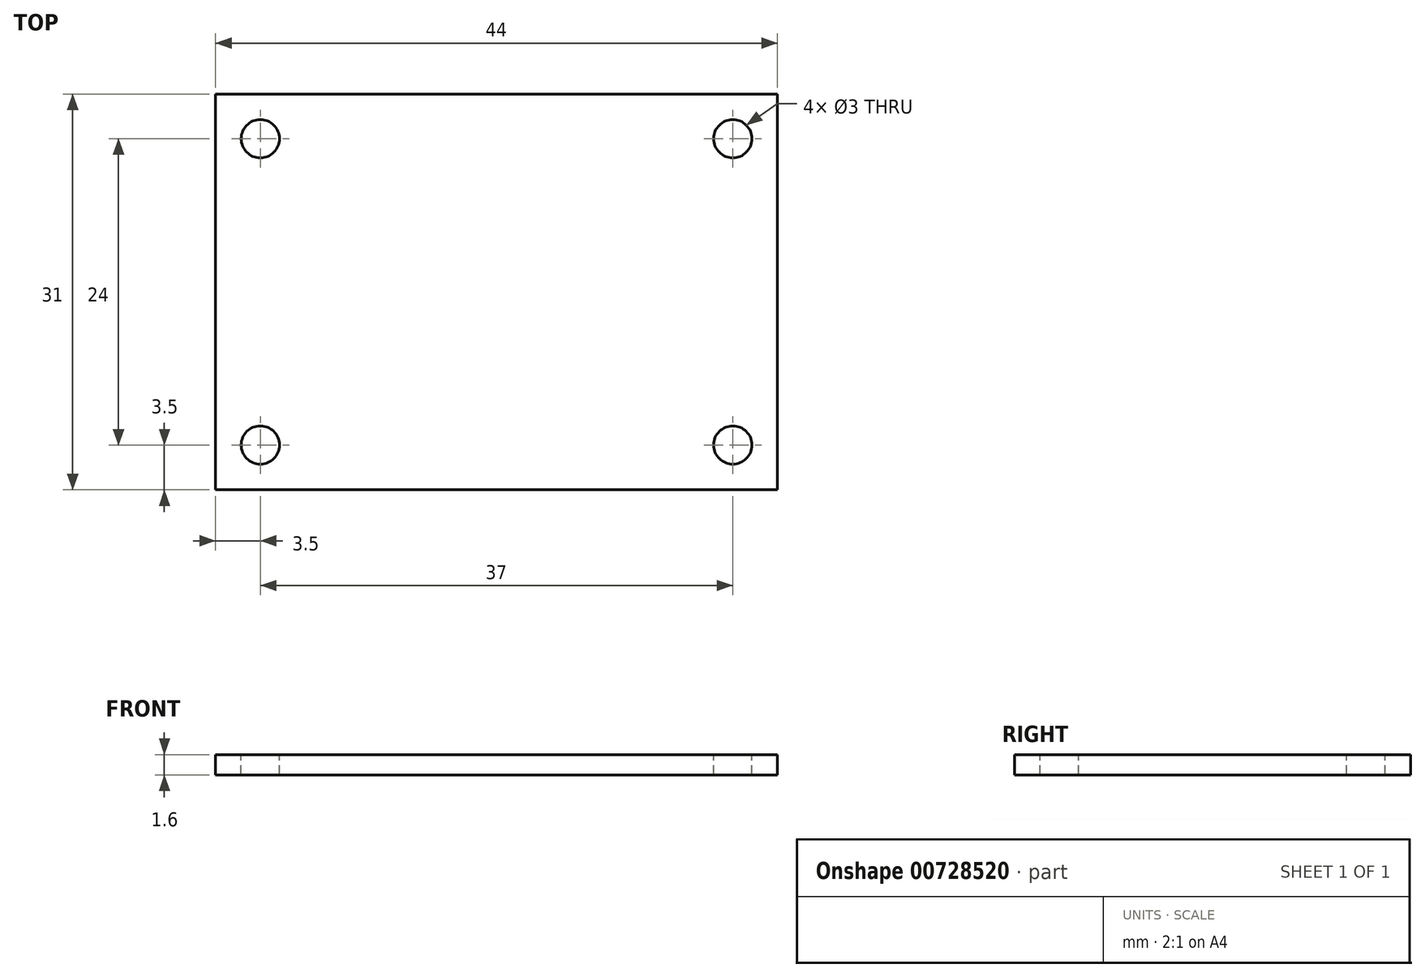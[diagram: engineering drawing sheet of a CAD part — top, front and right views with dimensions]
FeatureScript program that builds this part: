
annotation { "Feature Type Name" : "Feature", "Feature Type Description" : "" }
export const myFeature = defineFeature(function(context is Context, id is Id, definition is map)
    precondition{}
    {
        {
            var Q0;
            Q0=qCreatedBy(makeId("Top.planeOp"),FACE);
            var sketch = newSketch(context, id + "F0", { "sketchPlane" : qUnion([Q0])});
            skLineSegment(sketch, "E0.bottom", {"start": v(-44, 31) * mm, "end": v(0, 31) * mm});
            skLineSegment(sketch, "E0.top", {"start": v(-44, 0) * mm, "end": v(0, 0) * mm});
            skLineSegment(sketch, "E0.left", {"start": v(-44, 31) * mm, "end": v(-44, 0) * mm});
            skLineSegment(sketch, "E0.right", {"start": v(0, 31) * mm, "end": v(0, 0) * mm});
            skLineSegment(sketch, "E1", {"start": v(-22, 31) * mm, "end": v(-22, 0) * mm, "construction": true});
            skLineSegment(sketch, "E2", {"start": v(0, 15.5) * mm, "end": v(-44, 15.5) * mm, "construction": true});
            skCircle(sketch, "E3", {"center": v(-40.5, 27.5) * mm, "radius": 1.5 * mm});
            skCircle(sketch, "E4.MirrorC", {"center": v(-3.5, 27.5) * mm, "radius": 1.5 * mm});
            skCircle(sketch, "E5.MirrorC", {"center": v(-40.5, 3.5) * mm, "radius": 1.5 * mm});
            skCircle(sketch, "E6.MirrorC", {"center": v(-3.5, 3.5) * mm, "radius": 1.5 * mm});
            skPoint(sketch, "E7", {"position": v(-22, 15.5) * mm});
            skSolve(sketch);
        }
        {
            var Q0;
            Q0=qSketchRegion(id+"F0",true);
            extrude(context, id + "F1", {"entities" : qUnion([Q0]), "oppositeDirection" : true, "depth" : 1.6 * mm, "offsetDistance" : 25 * mm});
        }
    });
